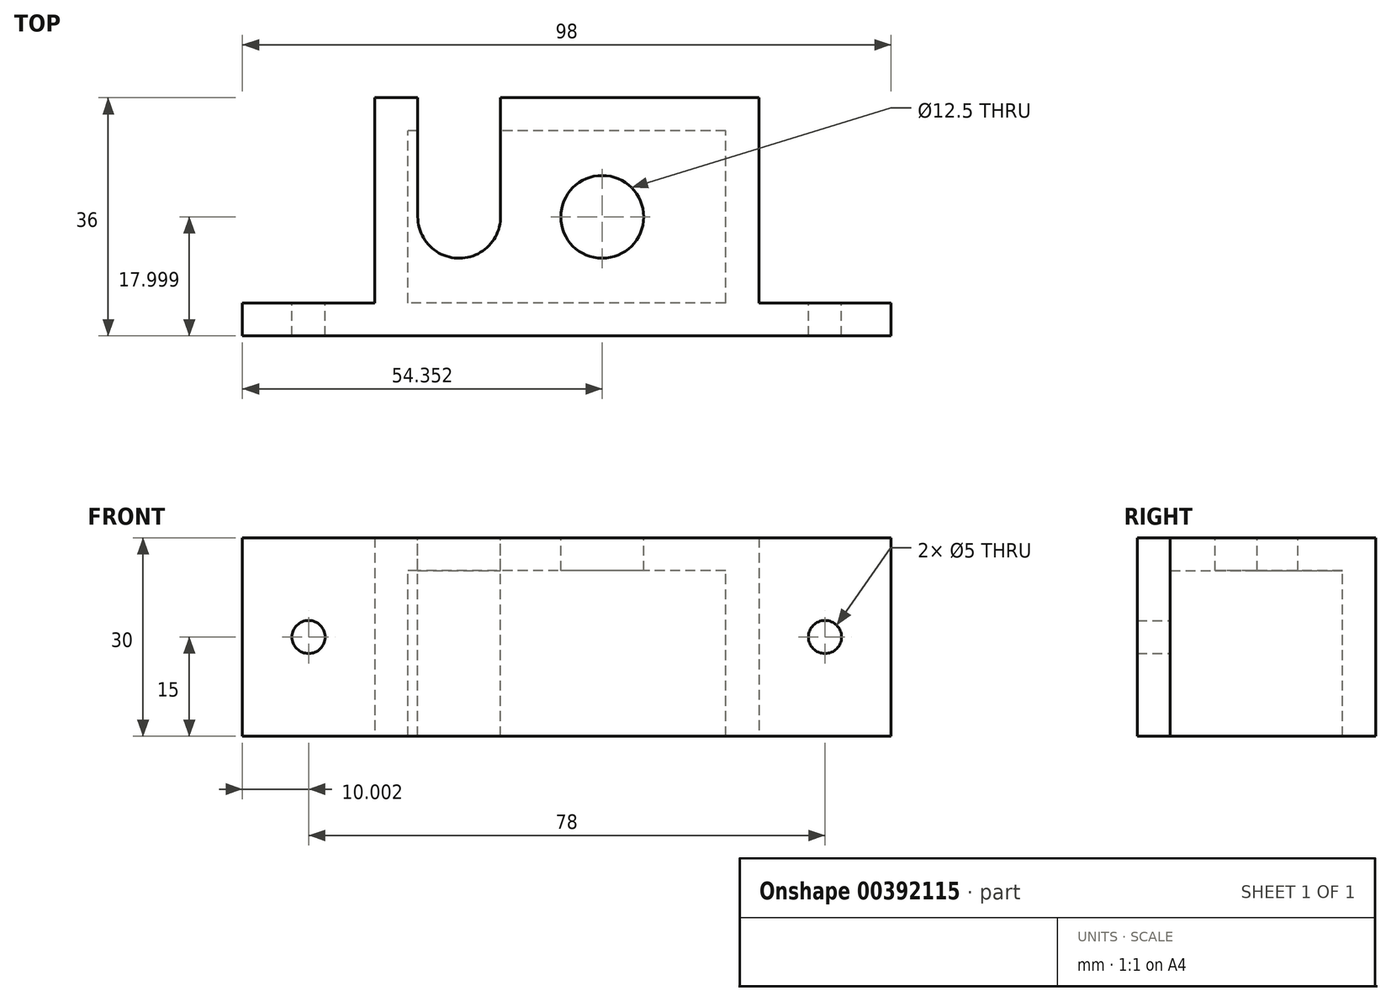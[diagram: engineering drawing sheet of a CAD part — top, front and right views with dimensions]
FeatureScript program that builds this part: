
annotation { "Feature Type Name" : "Feature", "Feature Type Description" : "" }
export const myFeature = defineFeature(function(context is Context, id is Id, definition is map)
    precondition{}
    {
        {
            var Q0;
            Q0=qCreatedBy(makeId("Top.planeOp"),FACE);
            var sketch = newSketch(context, id + "F0", { "sketchPlane" : qUnion([Q0])});
            skLineSegment(sketch, "E0.bottom", {"start": v(-22.68, 32.37) * mm, "end": v(-21.18, 32.37) * mm});
            skLineSegment(sketch, "E0.top", {"start": v(-22.68, 6.37) * mm, "end": v(25.32, 6.37) * mm});
            skLineSegment(sketch, "E0.left", {"start": v(-22.68, 32.37) * mm, "end": v(-22.68, 6.37) * mm});
            skLineSegment(sketch, "E0.right", {"start": v(25.32, 32.37) * mm, "end": v(25.32, 6.37) * mm});
            skCircle(sketch, "E1", {"center": v(6.67, 19.37) * mm, "radius": 6.25 * mm});
            skArc(sketch, "E2", {"start": v(-21.18, 19.37) * mm, "mid": v(-14.86, 13.12) * mm, "end": v(-8.68, 19.5) * mm});
            skLineSegment(sketch, "E3", {"start": v(-8.68, 19.5) * mm, "end": v(-8.68, 32.37) * mm});
            skLineSegment(sketch, "E4", {"start": v(-21.18, 19.37) * mm, "end": v(-21.18, 32.37) * mm});
            skPoint(sketch, "E4.startSnap0", {"position": v(-22.68, 19.37) * mm});
            skLineSegment(sketch, "E5.trimOffspring", {"start": v(-8.68, 32.37) * mm, "end": v(25.32, 32.37) * mm});
            skLineSegment(sketch, "E6", {"start": v(-8.68, 32.37) * mm, "end": v(-8.68, 37.37) * mm});
            skLineSegment(sketch, "E7", {"start": v(-8.68, 37.37) * mm, "end": v(30.32, 37.37) * mm});
            skLineSegment(sketch, "E8", {"start": v(30.32, 37.37) * mm, "end": v(30.32, 1.37) * mm});
            skLineSegment(sketch, "E9", {"start": v(30.32, 1.37) * mm, "end": v(-27.68, 1.37) * mm});
            skLineSegment(sketch, "E10", {"start": v(-27.68, 1.37) * mm, "end": v(-27.68, 37.37) * mm});
            skLineSegment(sketch, "E11", {"start": v(-27.68, 37.37) * mm, "end": v(-21.18, 37.37) * mm});
            skLineSegment(sketch, "E12", {"start": v(-21.18, 37.37) * mm, "end": v(-21.18, 32.37) * mm});
            skLineSegment(sketch, "E13", {"start": v(-22.68, 6.37) * mm, "end": v(-27.68, 6.37) * mm});
            skLineSegment(sketch, "E14", {"start": v(25.32, 6.37) * mm, "end": v(30.32, 6.37) * mm});
            skSolve(sketch);
        }
        {
            var Q0;
            Q0=makeQuery(id+"F0.imprint","IMPRINT",FACE,{"disambiguationData":[TD([[makeQuery(id+"F0.imprint","IMPRINT",EDGE,{"derivedFrom":sQuery(id+"F0.wireOp",EDGE,"E0.right")}),1.0]])]});
            var Q1;
            Q1=makeQuery(id+"F0.imprint","IMPRINT",FACE,{"disambiguationData":[TD([[makeQuery(id+"F0.imprint","IMPRINT",EDGE,{"derivedFrom":sQuery(id+"F0.wireOp",EDGE,"E0.bottom")}),1.0]])]});
            var Q2;
            Q2=makeQuery(id+"F0.imprint","IMPRINT",FACE,{"disambiguationData":[TD([[makeQuery(id+"F0.imprint","IMPRINT",EDGE,{"derivedFrom":sQuery(id+"F0.wireOp",EDGE,"E0.top")}),-1.0]])]});
            var Q3;
            Q3 = qSketchRegion(id + "F3", true);
            extrude(context, id + "F1", {"entities" : qUnion([Q0, Q1, Q2, Q3]), "oppositeDirection" : true, "depth" : 30 * mm});
        }
        {
            var Q0;
            Q0 = qSketchRegion(id + "F0", true);
            extrude(context, id + "F2", {"entities" : qUnion([Q0]), "operationType" : NewBodyOperationType.ADD, "oppositeDirection" : true, "depth" : 5 * mm});
        }
        {
            var Q0;
            Q0=makeQuery(id+"F1.opExtrude","SWEPT_FACE",FACE,{"disambiguationData":[OSD([sQuery(id+"F0.wireOp",EDGE,"E8")])]});
            var sketch = newSketch(context, id + "F3", { "sketchPlane" : qUnion([Q0])});
            skLineSegment(sketch, "E15.bottom", {"start": v(1.37, 0) * mm, "end": v(6.37, 0) * mm});
            skLineSegment(sketch, "E15.top", {"start": v(1.37, -30) * mm, "end": v(6.37, -30) * mm});
            skLineSegment(sketch, "E15.left", {"start": v(1.37, 0) * mm, "end": v(1.37, -30) * mm});
            skLineSegment(sketch, "E15.right", {"start": v(6.37, 0) * mm, "end": v(6.37, -30) * mm});
            skSolve(sketch);
        }
        {
            var Q0;
            Q0 = qSketchRegion(id + "F3", true);
            extrude(context, id + "F4", {"entities" : qUnion([Q0]), "operationType" : NewBodyOperationType.ADD, "depth" : 20 * mm});
        }
        {
            var Q0;
            Q0=makeQuery(id+"F1.opExtrude","SWEPT_FACE",FACE,{"disambiguationData":[OSD([sQuery(id+"F0.wireOp",EDGE,"E10")])]});
            var sketch = newSketch(context, id + "F5", { "sketchPlane" : qUnion([Q0])});
            skLineSegment(sketch, "E16.bottom", {"start": v(-6.37, 0) * mm, "end": v(-1.37, 0) * mm});
            skLineSegment(sketch, "E16.top", {"start": v(-6.37, -30) * mm, "end": v(-1.37, -30) * mm});
            skLineSegment(sketch, "E16.left", {"start": v(-6.37, 0) * mm, "end": v(-6.37, -30) * mm});
            skLineSegment(sketch, "E16.right", {"start": v(-1.37, 0) * mm, "end": v(-1.37, -30) * mm});
            skSolve(sketch);
        }
        {
            var Q0;
            Q0 = qSketchRegion(id + "F5", true);
            extrude(context, id + "F6", {"entities" : qUnion([Q0]), "operationType" : NewBodyOperationType.ADD, "depth" : 20 * mm});
        }
        {
            var Q0;
            Q0=makeQuery(id+"F4.opExtrude","SWEPT_FACE",FACE,{"disambiguationData":[OSD([sQuery(id+"F3.wireOp",EDGE,"E15.right")])]});
            var sketch = newSketch(context, id + "F7", { "sketchPlane" : qUnion([Q0])});
            skCircle(sketch, "E17", {"center": v(-40.32, -15) * mm, "radius": 2.5 * mm});
            skCircle(sketch, "E18", {"center": v(37.68, -15) * mm, "radius": 2.5 * mm});
            skSolve(sketch);
        }
        {
            var Q0;
            Q0 = qSketchRegion(id + "F7", true);
            extrude(context, id + "F8", {"entities" : qUnion([Q0]), "operationType" : NewBodyOperationType.REMOVE, "oppositeDirection" : true, "depth" : 25 * mm});
        }
    });
